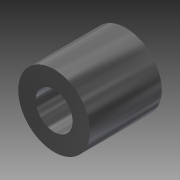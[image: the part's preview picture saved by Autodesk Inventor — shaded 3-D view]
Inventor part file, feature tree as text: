
AUTODESK INVENTOR PART (.ipt)
format: ipt  version: 2012 (Build 160160000, 160)  size: 85,504 bytes
history: native  units: in
note: dims shown in document units (in); Inventor stores cm internally (conversion verified against a paired STEP export)
features: extrude x1, sketch x1
ambient origin geometry x8: Origin, YZ Plane, XZ Plane, XY Plane, X Axis, Y Axis, Z Axis, Center Point
bodies: Solid1 (feature_tree)
feature tree (2):
  extrude  "Extrusion1"  Depth=0.1935in
  sketch  "Sketch1"  dims[d0=0.375in d1=0.1935in d2=0.375in d3=0.0in]
